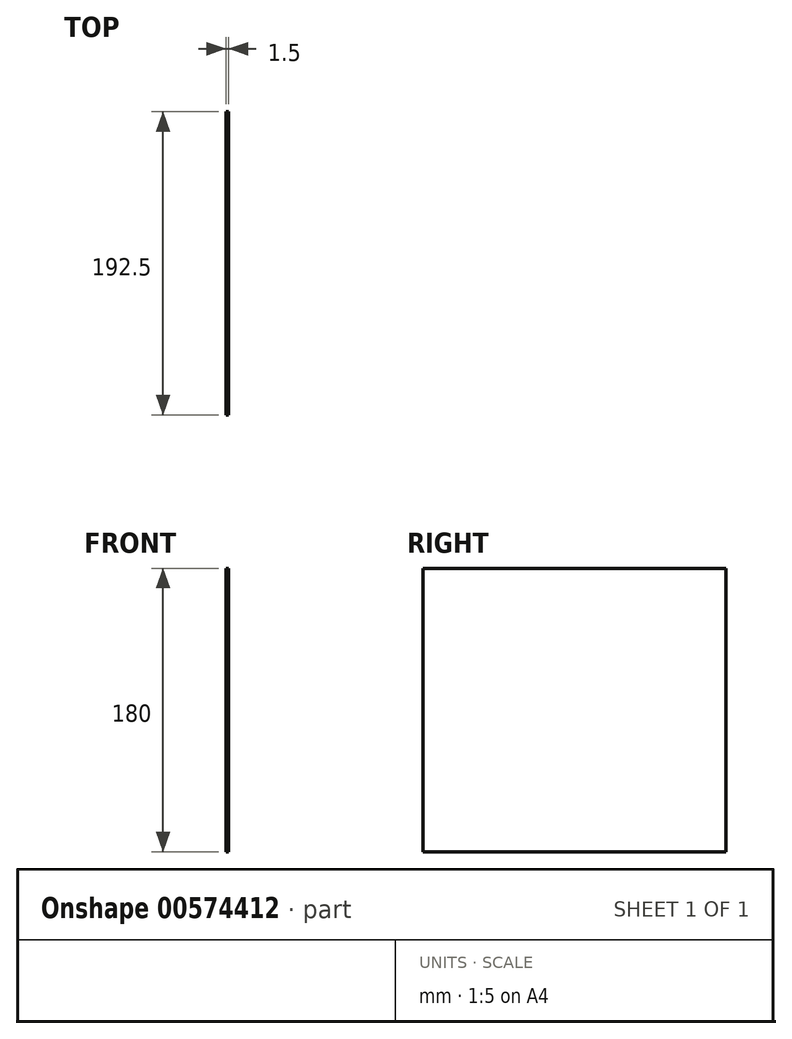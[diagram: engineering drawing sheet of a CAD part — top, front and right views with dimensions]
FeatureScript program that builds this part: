
annotation { "Feature Type Name" : "Feature", "Feature Type Description" : "" }
export const myFeature = defineFeature(function(context is Context, id is Id, definition is map)
    precondition{}
    {
        {
            var Q0;
            Q0=qCreatedBy(makeId("Right.planeOp"),FACE);
            var sketch = newSketch(context, id + "F0", { "sketchPlane" : qUnion([Q0])});
            skLineSegment(sketch, "E0.bottom", {"start": v(96.25, 90) * mm, "end": v(-96.25, 90) * mm});
            skLineSegment(sketch, "E0.top", {"start": v(96.25, -90) * mm, "end": v(-96.25, -90) * mm});
            skLineSegment(sketch, "E0.left", {"start": v(96.25, 90) * mm, "end": v(96.25, -90) * mm});
            skLineSegment(sketch, "E0.right", {"start": v(-96.25, 90) * mm, "end": v(-96.25, -90) * mm});
            skPoint(sketch, "E0.middle", {"position": v(0, 0) * mm});
            skSolve(sketch);
        }
        {
            var Q0;
            Q0 = qSketchRegion(id + "F0", true);
            extrude(context, id + "F1", {"entities" : qUnion([Q0]), "depth" : 1.5 * mm, "offsetDistance" : 25 * mm});
        }
    });
